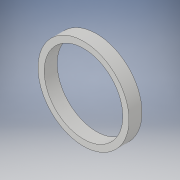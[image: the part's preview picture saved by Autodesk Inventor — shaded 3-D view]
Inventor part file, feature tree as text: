
AUTODESK INVENTOR PART (.ipt)
format: ipt  version: 2019 (Build 230136000, 136)  size: 104,960 bytes
history: native  units: mm
features: extrude x2, sketch x2
ambient origin geometry x8: Origin, YZ Plane, XZ Plane, XY Plane, X Axis, Y Axis, Z Axis, Center Point
bodies: Solid1 (feature_tree)
feature tree (4):
  extrude  "Extrusion1"  Depth=100.0mm TaperAngle=0.0deg
  extrude  "Extrusion2"  Depth=10.0mm TaperAngle=0.0deg
  sketch  "Sketch1"  dims[d0=700.0mm d1=100.0mm d2=0.0mm]
  sketch  "Sketch2"  dims[d3=605.0mm d4=10.0mm d5=0.0mm]
